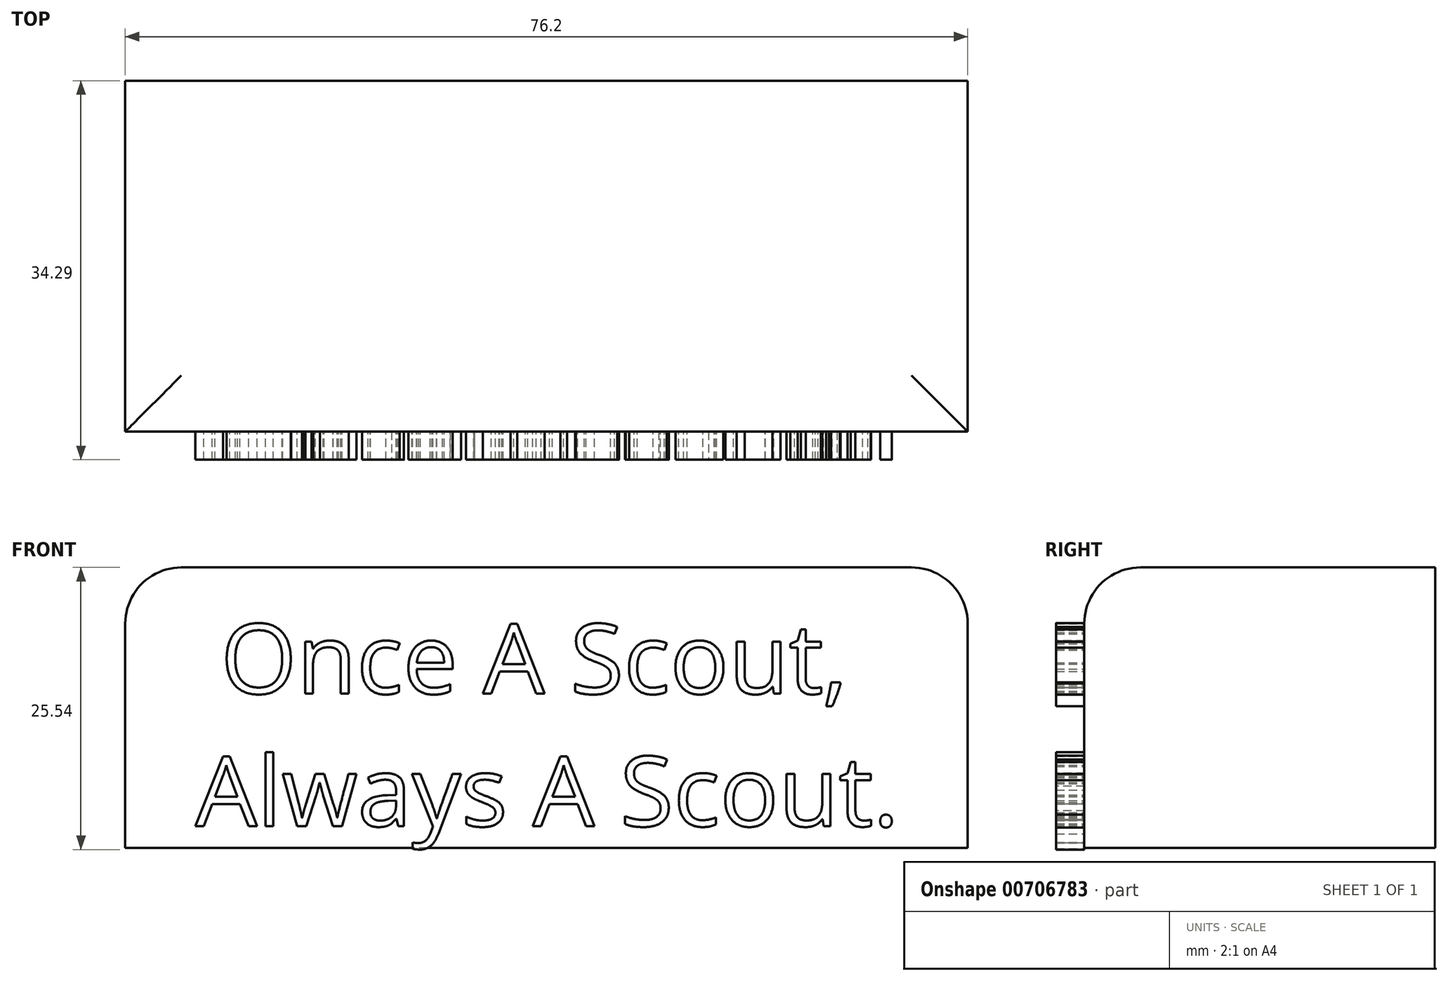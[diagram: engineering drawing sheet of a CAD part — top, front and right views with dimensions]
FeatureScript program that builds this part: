
annotation { "Feature Type Name" : "Feature", "Feature Type Description" : "" }
export const myFeature = defineFeature(function(context is Context, id is Id, definition is map)
    precondition{}
    {
        {
            var Q0;
            Q0=qCreatedBy(makeId("Top.planeOp"),FACE);
            var sketch = newSketch(context, id + "F0", { "sketchPlane" : qUnion([Q0])});
            skLineSegment(sketch, "E0.bottom", {"start": v(0, 0) * mm, "end": v(-76.2, 0) * mm});
            skLineSegment(sketch, "E0.top", {"start": v(0, 31.75) * mm, "end": v(-76.2, 31.75) * mm});
            skLineSegment(sketch, "E0.left", {"start": v(0, 0) * mm, "end": v(0, 31.75) * mm});
            skLineSegment(sketch, "E0.right", {"start": v(-76.2, 0) * mm, "end": v(-76.2, 31.75) * mm});
            skSolve(sketch);
        }
        {
            var Q0;
            Q0 = qSketchRegion(id + "F0", true);
            var Q1;
            Q1=makeQuery(id+"F0.imprint","IMPRINT",FACE,{"disambiguationData":[TD([[makeQuery(id+"F0.imprint","IMPRINT",EDGE,{"derivedFrom":sQuery(id+"F0.wireOp",EDGE,"E0.bottom")}),-1.0]])]});
            extrude(context, id + "F1", {"entities" : qUnion([Q0, Q1]), "depth" : 25.4 * mm, "offsetDistance" : 25.4 * mm});
        }
        {
            var Q0;
            Q0=makeQuery(id+"F1.opExtrude","CAP_EDGE",EDGE,{"disambiguationData":[OSD([sQuery(id+"F0.wireOp",EDGE,"E0.bottom")])],"isStart":false});
            var Q1;
            Q1=makeQuery(id+"F1.opExtrude","CAP_EDGE",EDGE,{"disambiguationData":[OSD([sQuery(id+"F0.wireOp",EDGE,"E0.right")])],"isStart":false});
            var Q2;
            Q2=makeQuery(id+"F1.opExtrude","CAP_EDGE",EDGE,{"disambiguationData":[OSD([sQuery(id+"F0.wireOp",EDGE,"E0.left")])],"isStart":false});
            fillet(context, id + "F2", {"entities" : qUnion([Q0, Q1, Q2]), "radius" : 5.08 * mm, "tangentPropagation" : true, "allowEdgeOverflow" : false});
        }
        {
            var Q0;
            Q0=makeQuery(id+"F1.opExtrude","SWEPT_FACE",FACE,{"disambiguationData":[OSD([sQuery(id+"F0.wireOp",EDGE,"E0.bottom")])]});
            var sketch = newSketch(context, id + "F3", { "sketchPlane" : qUnion([Q0])});
            skText(sketch, "E1", { "text": " Once A Scout,\nAlways A Scout.", "fontName": "OpenSans-Regular.ttf"});
            const initialGuessF3  = {"E1": [-0.06985, 0.01397, 1, 0, 0.00635]};
            skSetInitialGuess(sketch, initialGuessF3);
            skSolve(sketch);
        }
        {
            var Q0;
            Q0 = qSketchRegion(id + "F3", true);
            extrude(context, id + "F4", {"entities" : qUnion([Q0]), "operationType" : NewBodyOperationType.ADD, "depth" : 2.54 * mm, "offsetDistance" : 25.4 * mm});
        }
    });
